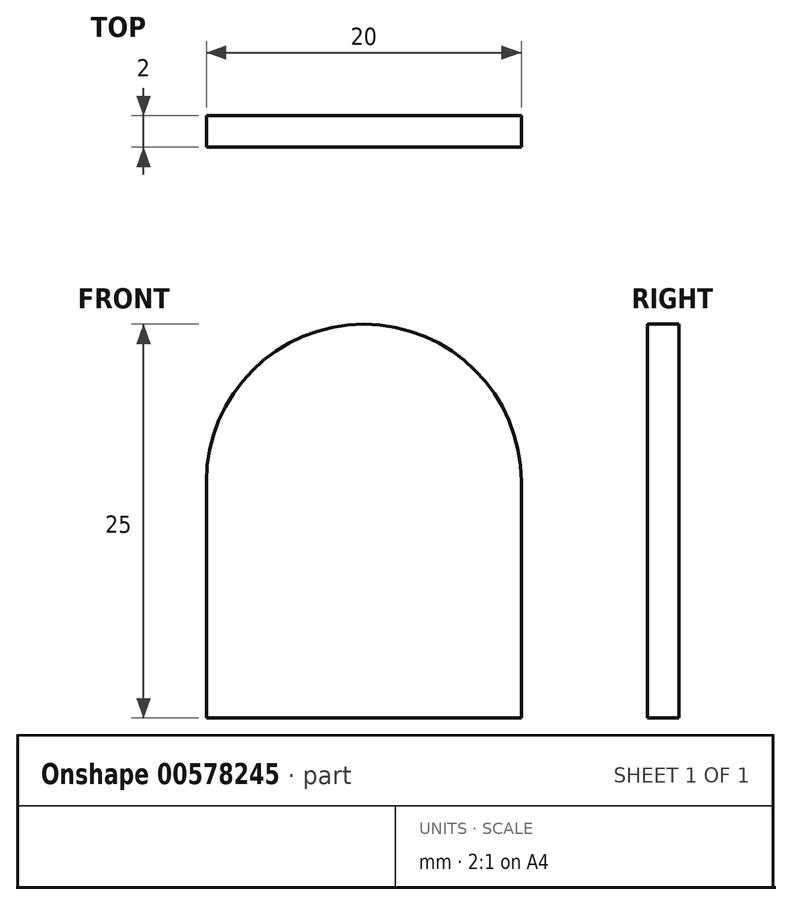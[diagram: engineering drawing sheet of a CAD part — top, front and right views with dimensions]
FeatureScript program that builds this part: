
annotation { "Feature Type Name" : "Feature", "Feature Type Description" : "" }
export const myFeature = defineFeature(function(context is Context, id is Id, definition is map)
    precondition{}
    {
        {
            var Q0;
            Q0=qCreatedBy(makeId("Front.planeOp"),FACE);
            var sketch = newSketch(context, id + "F0", { "sketchPlane" : qUnion([Q0])});
            skCircle(sketch, "E0", {"center": v(0, 0) * mm, "radius": 10 * mm});
            skLineSegment(sketch, "E1", {"start": v(-10, 0) * mm, "end": v(-10, -15) * mm});
            skLineSegment(sketch, "E2", {"start": v(10, 0) * mm, "end": v(10, -15) * mm});
            skLineSegment(sketch, "E3", {"start": v(-10, -15) * mm, "end": v(10, -15) * mm});
            skSolve(sketch);
        }
        {
            var Q0;
            {var subQ0=sQuery(id+"F0.wireOp",EDGE,"E1");Q0=makeQuery(id+"F0.imprint","IMPRINT",FACE,{"disambiguationData":[TD([[makeQuery(id+"F0.imprint","IMPRINT",EDGE,{"derivedFrom":subQ0}),1.0]])]});}
            var Q1;
            {var subQ0=sQuery(id+"F0.wireOp",EDGE,"E0");var subQ1=makeQuery(id+"F0.imprint","INTERSECT",VERTEX,{"derivedFrom":[subQ0,sQuery(id+"F0.wireOp",EDGE,"E1")]});Q1=makeQuery(id+"F0.imprint","IMPRINT",FACE,{"disambiguationData":[TD([[makeQuery(id+"F0.imprint","IMPRINT",EDGE,{"disambiguationData":[TD([[subQ1,1.0]])],"derivedFrom":subQ0}),1.0]])]});}
            extrude(context, id + "F1", {"entities" : qUnion([Q0, Q1]), "depth" : 2 * mm, "offsetDistance" : 25 * mm});
        }
    });
